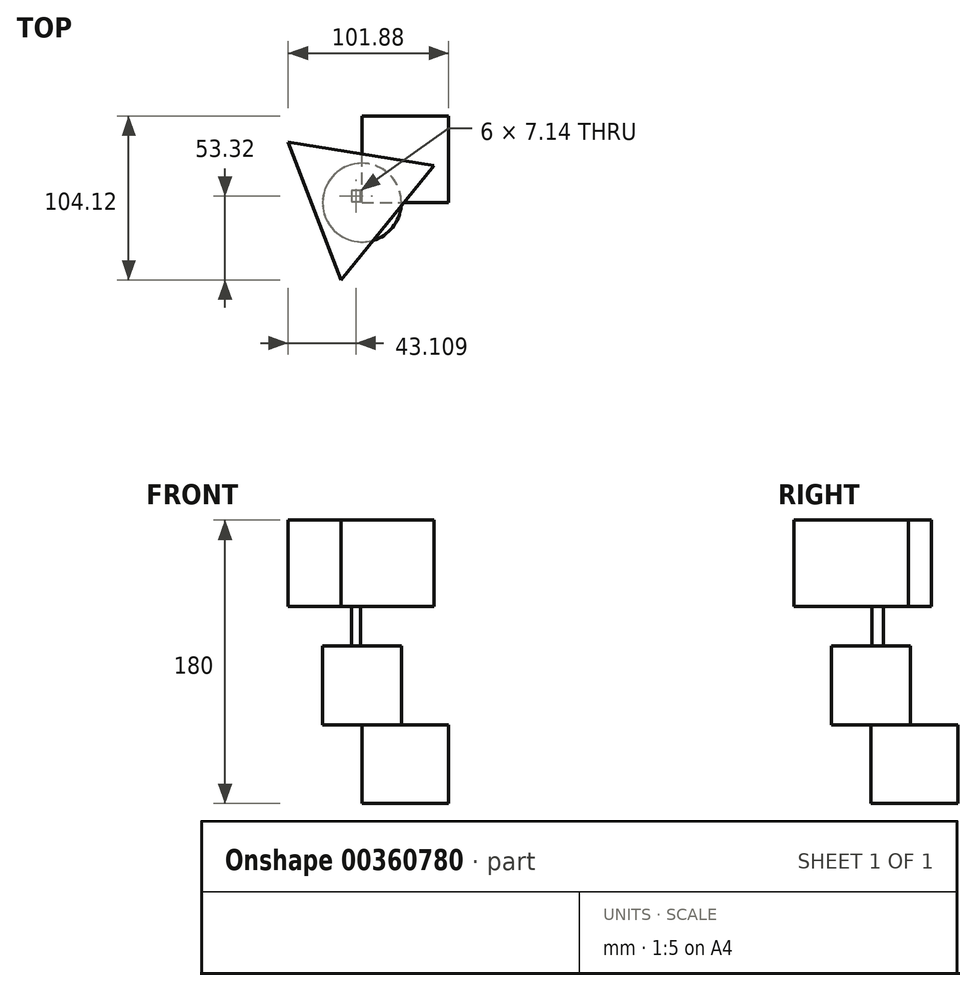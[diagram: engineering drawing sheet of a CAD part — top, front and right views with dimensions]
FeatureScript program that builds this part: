
annotation { "Feature Type Name" : "Feature", "Feature Type Description" : "" }
export const myFeature = defineFeature(function(context is Context, id is Id, definition is map)
    precondition{}
    {
        {
            var Q0;
            Q0=qCreatedBy(makeId("Top.planeOp"),FACE);
            var sketch = newSketch(context, id + "F0", { "sketchPlane" : qUnion([Q0])});
            skLineSegment(sketch, "E0.bottom", {"start": v(0, 0) * mm, "end": v(55, 0) * mm});
            skLineSegment(sketch, "E0.top", {"start": v(0, 55) * mm, "end": v(55, 55) * mm});
            skLineSegment(sketch, "E0.left", {"start": v(0, 0) * mm, "end": v(0, 55) * mm});
            skLineSegment(sketch, "E0.right", {"start": v(55, 0) * mm, "end": v(55, 55) * mm});
            skSolve(sketch);
        }
        {
            var Q0;
            Q0 = qSketchRegion(id + "F0", true);
            extrude(context, id + "F1", {"entities" : qUnion([Q0]), "depth" : 50 * mm});
        }
        {
            var Q0;
            Q0=makeQuery(id+"F1.opExtrude","CAP_FACE",FACE,{"disambiguationData":[OSD([sQuery(id+"F0.wireOp",EDGE,"E0.bottom"),sQuery(id+"F0.wireOp",EDGE,"E0.top"),sQuery(id+"F0.wireOp",EDGE,"E0.left"),sQuery(id+"F0.wireOp",EDGE,"E0.right")])],"isStart":false});
            var sketch = newSketch(context, id + "F2", { "sketchPlane" : qUnion([Q0])});
            skCircle(sketch, "E1", {"center": v(0, 0) * mm, "radius": 25 * mm});
            skSolve(sketch);
        }
        {
            var Q0;
            Q0 = qSketchRegion(id + "F2", true);
            extrude(context, id + "F3", {"entities" : qUnion([Q0]), "operationType" : NewBodyOperationType.ADD, "depth" : 50 * mm});
        }
        {
            var Q0;
            Q0=makeQuery(id+"F3.opExtrude","CAP_FACE",FACE,{"disambiguationData":[OSD([sQuery(id+"F2.wireOp",EDGE,"E1")])],"isStart":false});
            var sketch = newSketch(context, id + "F4", { "sketchPlane" : qUnion([Q0])});
            skText(sketch, "E2", { "text": "東", "fontName": "OpenSans-Regular.ttf"});
            const initialGuessF4  = {"E2": [-0.0073, 0, 1, 0, 0.0084]};
            skSetInitialGuess(sketch, initialGuessF4);
            skSolve(sketch);
        }
        {
            var Q0;
            Q0 = qSketchRegion(id + "F4", true);
            extrude(context, id + "F5", {"entities" : qUnion([Q0]), "operationType" : NewBodyOperationType.ADD, "depth" : 25 * mm});
        }
        {
            var Q0;
            Q0=makeQuery(id+"F5.opExtrude","CAP_FACE",FACE,{"disambiguationData":[OSD([sQuery(id+"F4.wireOp",EDGE,"E2.sketch_text.stroke-0"),sQuery(id+"F4.wireOp",EDGE,"E2.sketch_text.stroke-1"),sQuery(id+"F4.wireOp",EDGE,"E2.sketch_text.stroke-2"),sQuery(id+"F4.wireOp",EDGE,"E2.sketch_text.stroke-3")])],"isStart":false});
            var sketch = newSketch(context, id + "F6", { "sketchPlane" : qUnion([Q0])});
            skCircle(sketch, "E3.cCircle", {"center": v(-4.88, 4.31) * mm, "radius": 27.06 * mm, "construction": true});
            skLineSegment(sketch, "E3.0", {"start": v(45.68, 23.62) * mm, "end": v(-13.43, -49.12) * mm});
            skLineSegment(sketch, "E3.1", {"start": v(-13.43, -49.12) * mm, "end": v(-46.88, 38.44) * mm});
            skLineSegment(sketch, "E3.2", {"start": v(-46.88, 38.44) * mm, "end": v(45.68, 23.62) * mm});
            skPoint(sketch, "E3.0.midPoint", {"position": v(16.13, -12.75) * mm});
            skSolve(sketch);
        }
        {
            var Q0;
            Q0 = qSketchRegion(id + "F6", true);
            extrude(context, id + "F7", {"entities" : qUnion([Q0]), "operationType" : NewBodyOperationType.ADD, "depth" : 55 * mm});
        }
    });
